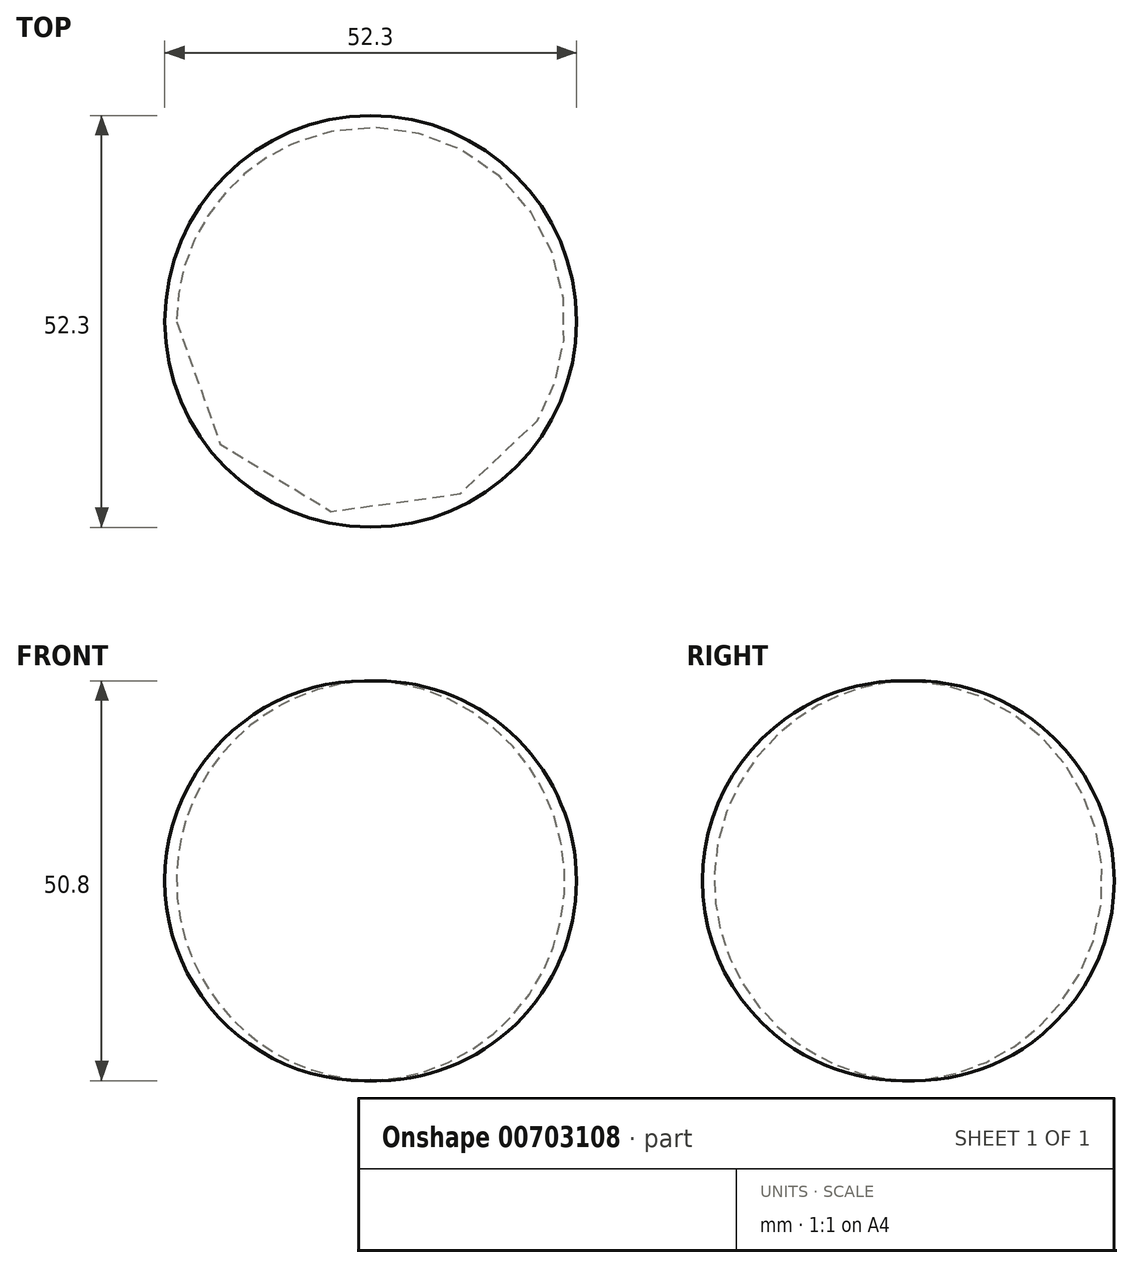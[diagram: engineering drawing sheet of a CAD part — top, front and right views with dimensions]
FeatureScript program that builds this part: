
annotation { "Feature Type Name" : "Feature", "Feature Type Description" : "" }
export const myFeature = defineFeature(function(context is Context, id is Id, definition is map)
    precondition{}
    {
        {
            var Q0;
            Q0=qCreatedBy(makeId("Front.planeOp"),FACE);
            var sketch = newSketch(context, id + "F0", { "sketchPlane" : qUnion([Q0])});
            skArc(sketch, "E0", {"start": v(-16.7, -13.07) * mm, "mid": v(9.46, 12.32) * mm, "end": v(-16.7, 37.7) * mm});
            skLineSegment(sketch, "E1", {"start": v(-16.7, 37.7) * mm, "end": v(-16.7, -13.07) * mm});
            skSolve(sketch);
        }
        {
            var Q0;
            Q0=makeQuery(id+"F0.imprint","IMPRINT",FACE,{"disambiguationData":[TD([[makeQuery(id+"F0.imprint","IMPRINT",EDGE,{"derivedFrom":sQuery(id+"F0.wireOp",EDGE,"E0")}),1.0]])]});
            var Q1;
            Q1=sQuery(id+"F0.wireOp",EDGE,"E1");
            revolve(context, id + "F1", {"surfaceOperationType" : NewSurfaceOperationType.NEW, "entities" : qUnion([Q0]), "axis" : qUnion([Q1]), "revolveType" : RevolveType.FULL});
        }
    });
